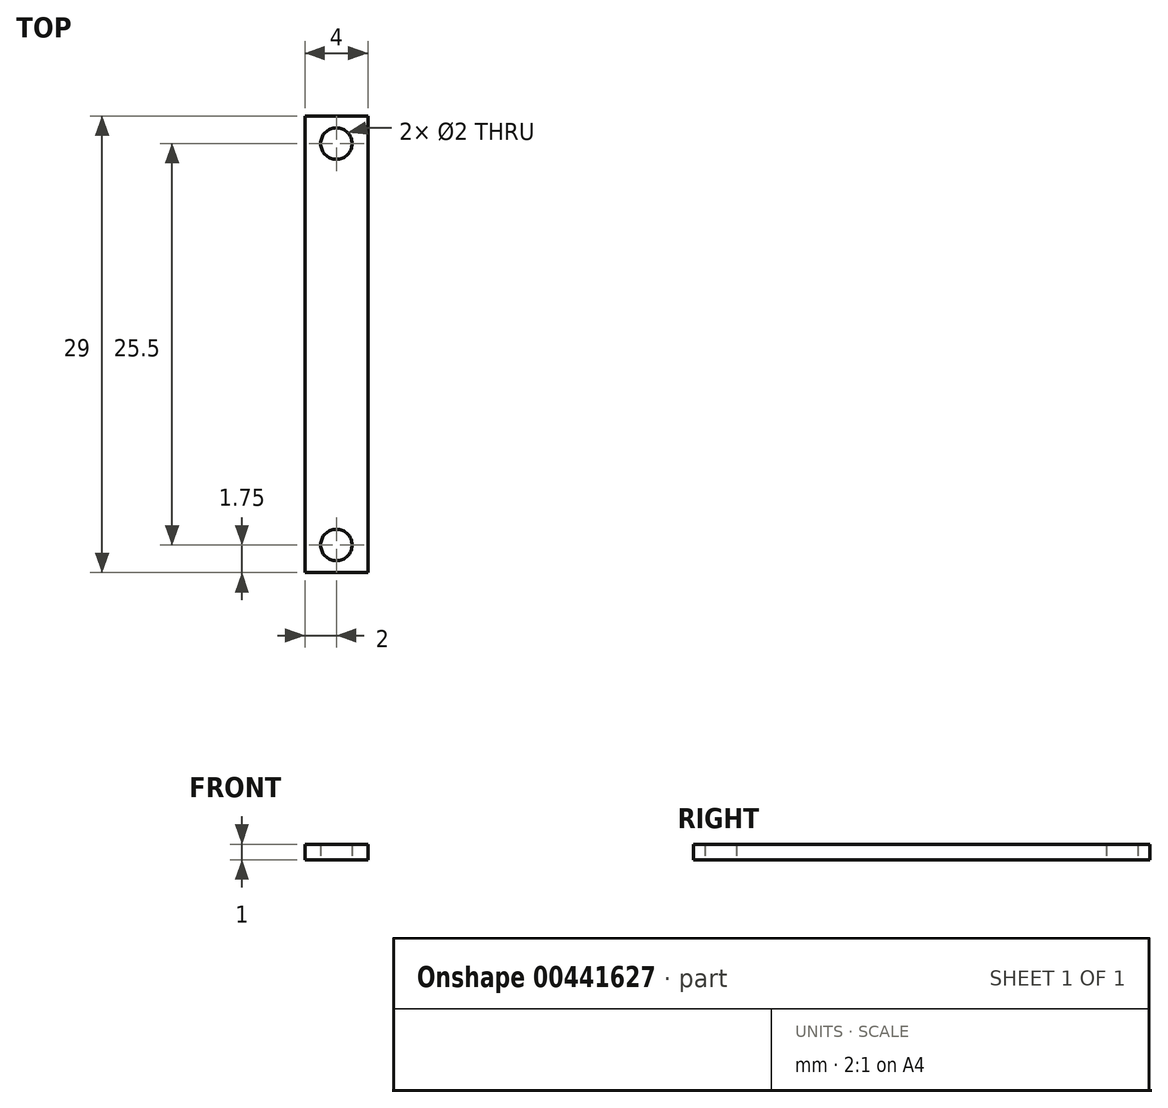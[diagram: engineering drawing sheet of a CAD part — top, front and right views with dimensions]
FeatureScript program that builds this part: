
annotation { "Feature Type Name" : "Feature", "Feature Type Description" : "" }
export const myFeature = defineFeature(function(context is Context, id is Id, definition is map)
    precondition{}
    {
        {
            var Q0;
            Q0=qCreatedBy(makeId("Top.planeOp"),FACE);
            var sketch = newSketch(context, id + "F0", { "sketchPlane" : qUnion([Q0])});
            skLineSegment(sketch, "E0.bottom", {"start": v(0, 0) * mm, "end": v(4, 0) * mm});
            skLineSegment(sketch, "E0.top", {"start": v(0, 29) * mm, "end": v(4, 29) * mm});
            skLineSegment(sketch, "E0.left", {"start": v(0, 0) * mm, "end": v(0, 29) * mm});
            skLineSegment(sketch, "E0.right", {"start": v(4, 0) * mm, "end": v(4, 29) * mm});
            skCircle(sketch, "E1", {"center": v(2, 27.25) * mm, "radius": 1 * mm});
            skPoint(sketch, "E1.centerSnap0", {"position": v(2, 29) * mm});
            skCircle(sketch, "E2", {"center": v(2, 1.75) * mm, "radius": 1 * mm});
            skPoint(sketch, "E2.centerSnap0", {"position": v(2, 0) * mm});
            skLineSegment(sketch, "E3", {"start": v(2, 27.25) * mm, "end": v(2, 29) * mm, "construction": true});
            skLineSegment(sketch, "E4", {"start": v(2, 1.75) * mm, "end": v(2, 0) * mm, "construction": true});
            skSolve(sketch);
        }
        {
            var Q0;
            Q0=makeQuery(id+"F0.imprint","IMPRINT",FACE,{"disambiguationData":[TD([[makeQuery(id+"F0.imprint","IMPRINT",EDGE,{"derivedFrom":sQuery(id+"F0.wireOp",EDGE,"E0.bottom")}),1.0]])]});
            extrude(context, id + "F1", {"entities" : qUnion([Q0]), "depth" : 1 * mm});
        }
    });
